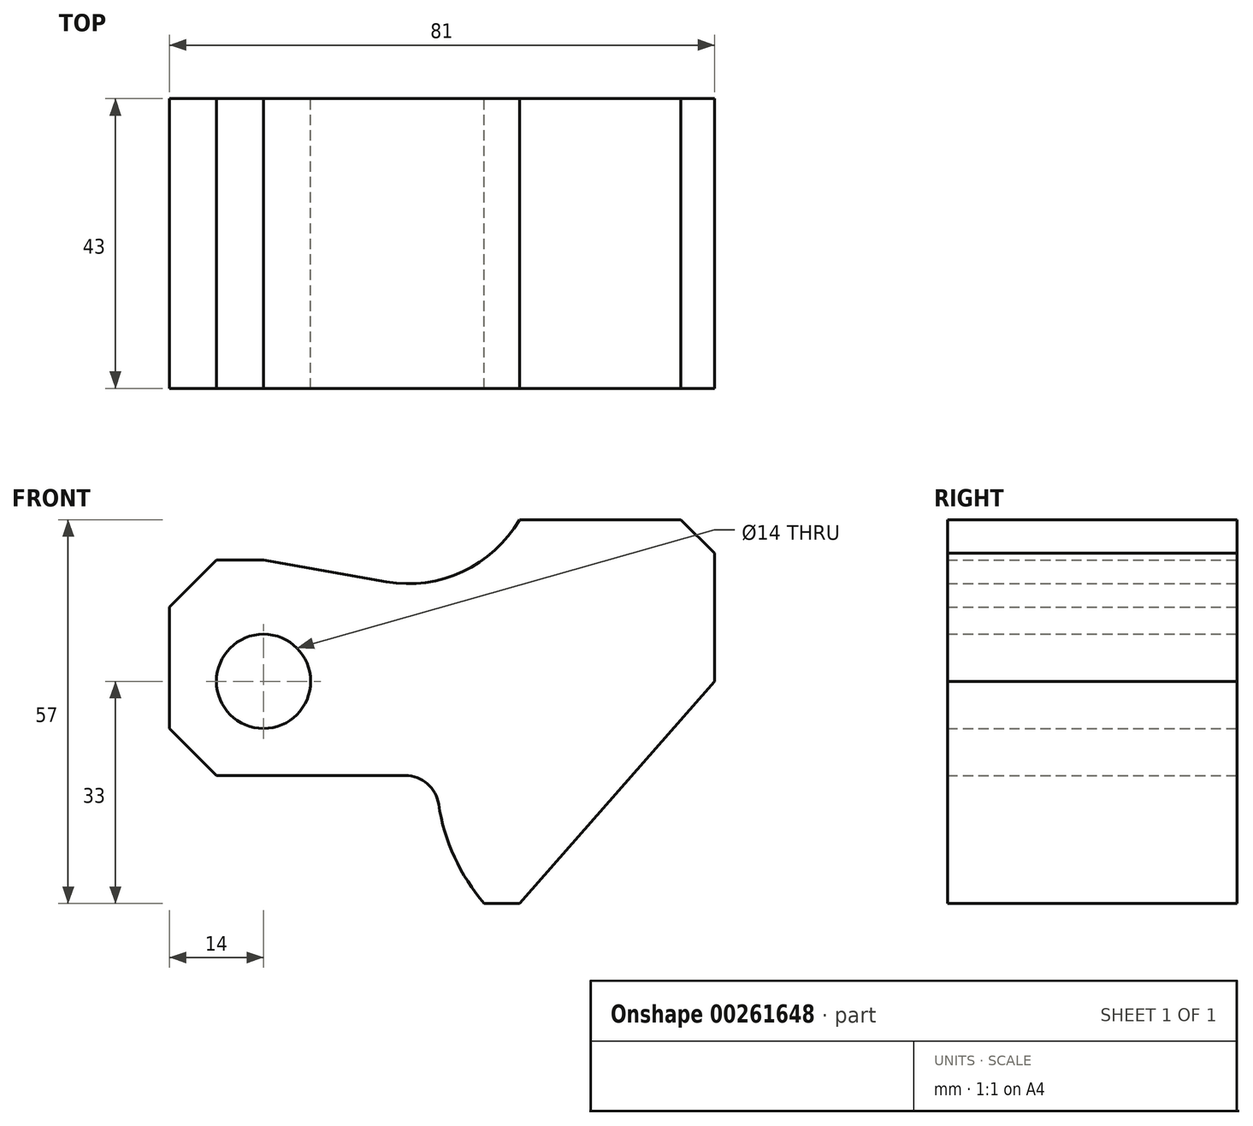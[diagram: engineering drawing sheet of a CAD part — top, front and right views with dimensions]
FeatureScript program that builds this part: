
annotation { "Feature Type Name" : "Feature", "Feature Type Description" : "" }
export const myFeature = defineFeature(function(context is Context, id is Id, definition is map)
    precondition{}
    {
        {
            var Q0;
            Q0=qCreatedBy(makeId("Front.planeOp"),FACE);
            var sketch = newSketch(context, id + "F0", { "sketchPlane" : qUnion([Q0])});
            skCircle(sketch, "E0", {"center": v(0, 0) * mm, "radius": 7 * mm});
            skLineSegment(sketch, "E1.top", {"start": v(21.07, -14) * mm, "end": v(-7, -14) * mm});
            skLineSegment(sketch, "E1.right", {"start": v(-14, 11) * mm, "end": v(-14, -7) * mm});
            skLineSegment(sketch, "E2", {"start": v(-14, -7) * mm, "end": v(-7, -14) * mm});
            skPoint(sketch, "E3.orphan", {"position": v(-14, -14) * mm});
            skLineSegment(sketch, "E4", {"start": v(-14, 11) * mm, "end": v(-7, 18) * mm});
            skPoint(sketch, "E5.orphan", {"position": v(-14, 18.98) * mm});
            skLineSegment(sketch, "E6", {"start": v(67, 0) * mm, "end": v(38, -33) * mm});
            skLineSegment(sketch, "E7", {"start": v(67, 0) * mm, "end": v(67, 19) * mm});
            skLineSegment(sketch, "E8", {"start": v(62, 24) * mm, "end": v(38, 24) * mm});
            skLineSegment(sketch, "E9", {"start": v(67, 19) * mm, "end": v(62, 24) * mm});
            skPoint(sketch, "E10.orphan", {"position": v(67, 24) * mm});
            skArc(sketch, "E11", {"start": v(26.01, -18.26) * mm, "mid": v(28.35, -26.12) * mm, "end": v(32.79, -33) * mm});
            skLineSegment(sketch, "E12", {"start": v(38, -33) * mm, "end": v(32.79, -33) * mm});
            skPoint(sketch, "E13.end.orphan", {"position": v(67, -33) * mm});
            skArc(sketch, "E14", {"start": v(26.01, -18.26) * mm, "mid": v(24.33, -15.21) * mm, "end": v(21.07, -14) * mm});
            skLineSegment(sketch, "E15", {"start": v(26.01, -18.26) * mm, "end": v(26.01, -18.26) * mm});
            skLineSegment(sketch, "E16", {"start": v(-7, 18) * mm, "end": v(0, 18) * mm});
            skLineSegment(sketch, "E17", {"start": v(0, 18) * mm, "end": v(18.24, 14.78) * mm});
            skArc(sketch, "E18", {"start": v(18.24, 14.78) * mm, "mid": v(29.57, 16.28) * mm, "end": v(38, 24) * mm});
            skSolve(sketch);
        }
        {
            var Q0;
            Q0 = qSketchRegion(id + "F0", true);
            extrude(context, id + "F1", {"entities" : qUnion([Q0]), "depth" : 43 * mm});
        }
    });
